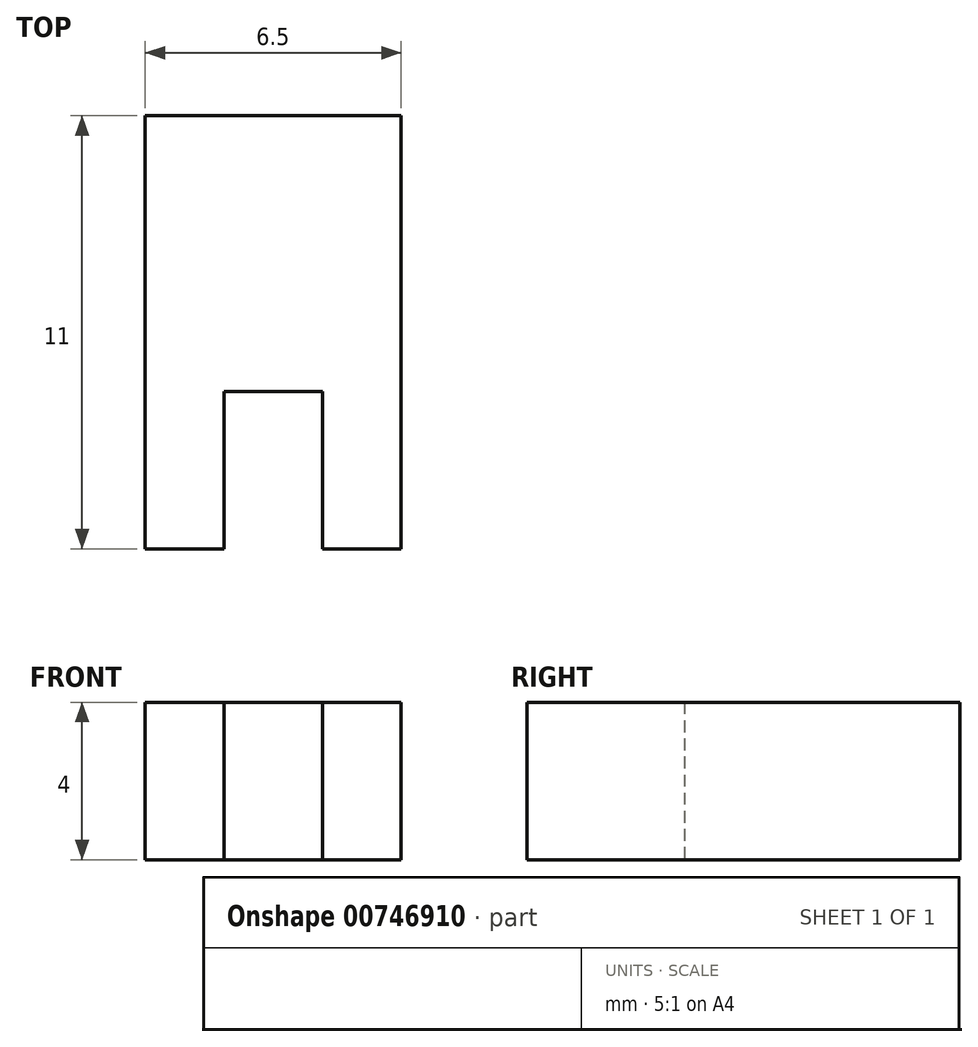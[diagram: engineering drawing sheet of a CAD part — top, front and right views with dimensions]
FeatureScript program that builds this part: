
annotation { "Feature Type Name" : "Feature", "Feature Type Description" : "" }
export const myFeature = defineFeature(function(context is Context, id is Id, definition is map)
    precondition{}
    {
        {
            var Q0;
            Q0=qCreatedBy(makeId("Top.planeOp"),FACE);
            var sketch = newSketch(context, id + "F0", { "sketchPlane" : qUnion([Q0])});
            skLineSegment(sketch, "E0", {"start": v(0, 0) * mm, "end": v(0, 11) * mm});
            skLineSegment(sketch, "E1", {"start": v(0, 11) * mm, "end": v(6.5, 11) * mm});
            skLineSegment(sketch, "E2", {"start": v(6.5, 11) * mm, "end": v(6.5, 0) * mm});
            skLineSegment(sketch, "E3", {"start": v(6.5, 0) * mm, "end": v(4.5, 0) * mm});
            skLineSegment(sketch, "E4", {"start": v(4.5, 0) * mm, "end": v(4.5, 4) * mm});
            skLineSegment(sketch, "E5", {"start": v(4.5, 4) * mm, "end": v(2, 4) * mm});
            skLineSegment(sketch, "E6", {"start": v(2, 4) * mm, "end": v(2, 0) * mm});
            skLineSegment(sketch, "E7", {"start": v(2, 0) * mm, "end": v(0, 0) * mm});
            skSolve(sketch);
        }
        {
            var Q0;
            Q0 = qSketchRegion(id + "F0", true);
            extrude(context, id + "F1", {"entities" : qUnion([Q0]), "depth" : 4 * mm, "offsetDistance" : 25 * mm});
        }
    });
